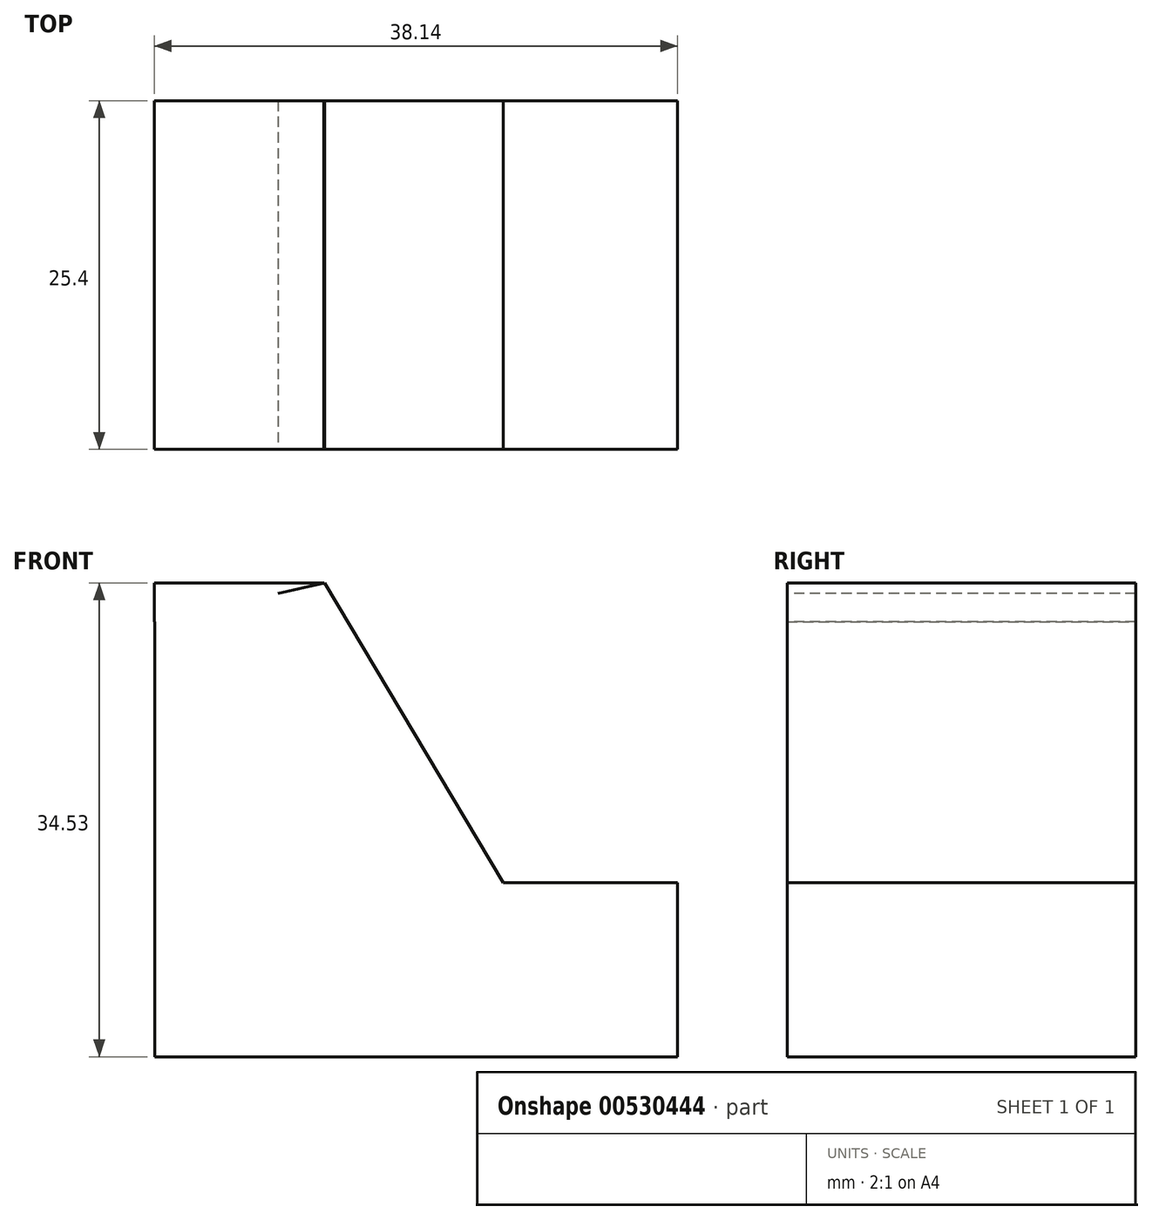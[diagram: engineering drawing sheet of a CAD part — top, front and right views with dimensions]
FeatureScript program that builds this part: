
annotation { "Feature Type Name" : "Feature", "Feature Type Description" : "" }
export const myFeature = defineFeature(function(context is Context, id is Id, definition is map)
    precondition{}
    {
        {
            var Q0;
            Q0=qCreatedBy(makeId("Front.planeOp"),FACE);
            var sketch = newSketch(context, id + "F0", { "sketchPlane" : qUnion([Q0])});
            skLineSegment(sketch, "E0", {"start": v(-33.67, 26.17) * mm, "end": v(-33.67, -5.58) * mm});
            skLineSegment(sketch, "E1", {"start": v(4.43, -5.58) * mm, "end": v(-33.67, -5.58) * mm});
            skLineSegment(sketch, "E2", {"start": v(4.43, -5.58) * mm, "end": v(4.43, 7.12) * mm});
            skLineSegment(sketch, "E3", {"start": v(4.43, 7.12) * mm, "end": v(-8.27, 7.12) * mm});
            skLineSegment(sketch, "E4", {"start": v(-8.27, 7.12) * mm, "end": v(-21.28, 28.94) * mm});
            skLineSegment(sketch, "E5", {"start": v(-33.67, 26.17) * mm, "end": v(-21.28, 28.94) * mm});
            skSolve(sketch);
        }
        {
            var Q0;
            Q0 = qSketchRegion(id + "F0", true);
            extrude(context, id + "F1", {"entities" : qUnion([Q0]), "depth" : 25.4 * mm, "offsetDistance" : 25.4 * mm});
        }
        {
            var Q0;
            Q0=makeQuery(id+"F1.opExtrude","CAP_FACE",FACE,{"disambiguationData":[OSD([sQuery(id+"F0.wireOp",EDGE,"E0"),sQuery(id+"F0.wireOp",EDGE,"E1"),sQuery(id+"F0.wireOp",EDGE,"E2"),sQuery(id+"F0.wireOp",EDGE,"E3"),sQuery(id+"F0.wireOp",EDGE,"E4"),sQuery(id+"F0.wireOp",EDGE,"E5")])],"isStart":false});
            extrude(context, id + "F2", {"entities" : qUnion([Q0]), "operationType" : NewBodyOperationType.ADD, "depth" : 25.4 * mm, "offsetDistance" : 25.4 * mm});
        }
        {
            var Q0;
            Q0=qCreatedBy(makeId("Front.planeOp"),FACE);
            var sketch = newSketch(context, id + "F3", { "sketchPlane" : qUnion([Q0])});
            skLineSegment(sketch, "E6", {"start": v(-21.33, 28.95) * mm, "end": v(-33.7, 28.95) * mm});
            skLineSegment(sketch, "E7", {"start": v(-33.7, 28.95) * mm, "end": v(-33.7, 26.12) * mm});
            skLineSegment(sketch, "E8", {"start": v(-33.7, 26.12) * mm, "end": v(-21.33, 28.95) * mm});
            skSolve(sketch);
        }
        {
            var Q0;
            Q0=makeQuery(id+"F3.imprint","IMPRINT",FACE,{"disambiguationData":[TD([[makeQuery(id+"F3.imprint","IMPRINT",EDGE,{"derivedFrom":sQuery(id+"F3.wireOp",EDGE,"E6")}),1.0]])]});
            extrude(context, id + "F4", {"entities" : qUnion([Q0]), "operationType" : NewBodyOperationType.ADD, "depth" : 25.4 * mm, "offsetDistance" : 25.4 * mm});
        }
        {
            var Q0;
            Q0=makeQuery(id+"F2.opExtrude","CAP_FACE",FACE,{"disambiguationData":[OSD([sQuery(id+"F0.wireOp",EDGE,"E0"),sQuery(id+"F0.wireOp",EDGE,"E1"),sQuery(id+"F0.wireOp",EDGE,"E2"),sQuery(id+"F0.wireOp",EDGE,"E3"),sQuery(id+"F0.wireOp",EDGE,"E4"),sQuery(id+"F0.wireOp",EDGE,"E5")])],"isStart":false});
            extrude(context, id + "F5", {"entities" : qUnion([Q0]), "operationType" : NewBodyOperationType.REMOVE, "oppositeDirection" : true, "depth" : 25.4 * mm, "offsetDistance" : 25.4 * mm});
        }
    });
